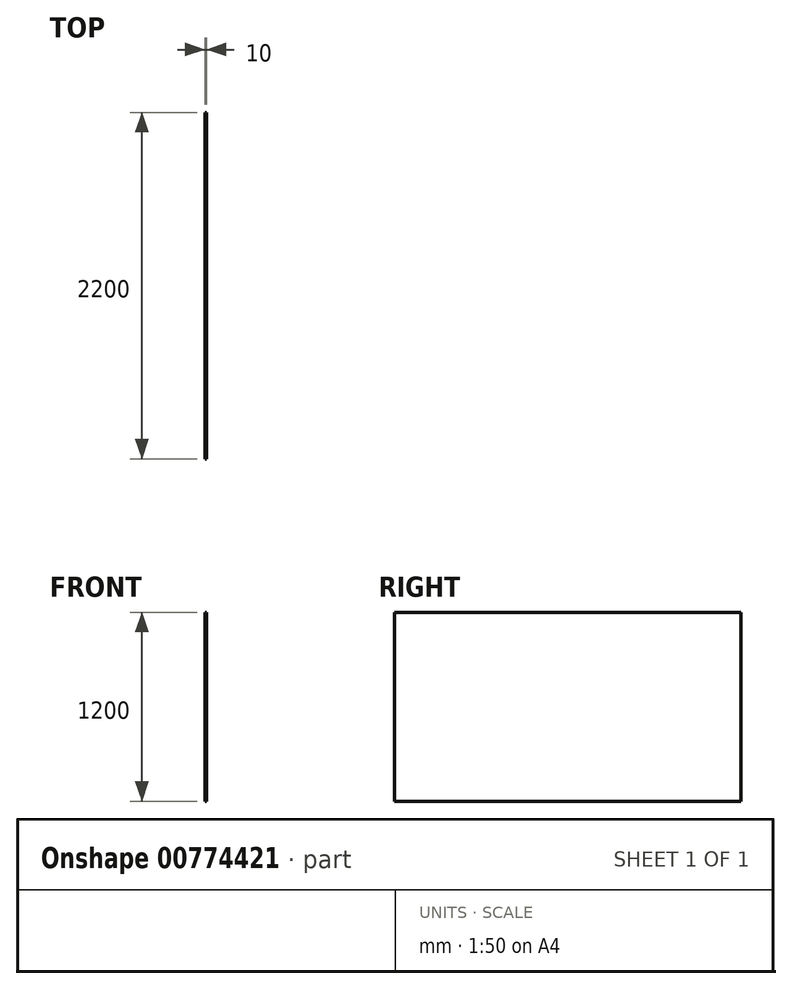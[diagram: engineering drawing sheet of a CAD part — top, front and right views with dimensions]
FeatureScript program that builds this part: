
annotation { "Feature Type Name" : "Feature", "Feature Type Description" : "" }
export const myFeature = defineFeature(function(context is Context, id is Id, definition is map)
    precondition{}
    {
        {
            var Q0;
            Q0=qCreatedBy(makeId("Front.planeOp"),FACE);
            var sketch = newSketch(context, id + "F0", { "sketchPlane" : qUnion([Q0])});
            skLineSegment(sketch, "E0", {"start": v(0, 0) * mm, "end": v(-10, 0) * mm});
            skLineSegment(sketch, "E1", {"start": v(-10, 0) * mm, "end": v(-10, 1200) * mm});
            skLineSegment(sketch, "E2", {"start": v(-10, 1200) * mm, "end": v(0, 1200) * mm});
            skLineSegment(sketch, "E3", {"start": v(0, 1200) * mm, "end": v(0, 0) * mm});
            skSolve(sketch);
        }
        {
            var Q0;
            Q0=qSketchRegion(id+"F0",true);
            extrude(context, id + "F1", {"entities" : qUnion([Q0]), "depth" : 2200 * mm, "offsetDistance" : 25 * mm});
        }
    });
